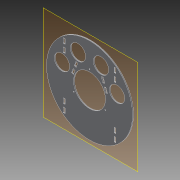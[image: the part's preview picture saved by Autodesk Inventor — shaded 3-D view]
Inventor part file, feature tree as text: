
AUTODESK INVENTOR PART (.ipt)
format: ipt  version: 2022 (Build 260153000, 153)  size: 220,160 bytes
history: native  units: mm
features: other x5, sketch x3, extrude x2, hole x1, pattern_circular x1, reference x1
ambient origin geometry x8: Origin, YZ Plane, XZ Plane, XY Plane, X Axis, Y Axis, Z Axis, Center Point
bodies: Body1 (feature_tree)
feature tree (13):
  other  "Твердое тело1"
  other  "РабПлоскость1"
  extrude  "Выдавливание1"  TaperAngle=90.0deg  [1 undecoded]
  hole  "Отверстие1"  [1 undecoded]
  pattern_circular  "Круговой массив1"  [2 undecoded]
  extrude  "Выдавливание2"  Depth=4.014257mm
  sketch  "Эскиз1"
  reference  "Ссылка1"
  sketch  "Эскиз2"
  sketch  "Эскиз3"
  parser-record x1  (decoder bookkeeping rows leaked as tree rows — omitted from the tree; the rows remain in map.json)
  other  "Поворотный_модуль_В5.iam"
  other  "Диск_опорный_В5:1"
note: 4 required parameter values undecoded (feature->parameter linkage not recoverable at this tier; creation-order binding heuristic only, values carry confidence <= 0.55)
note: 1 file-system path scrubbed to <path> (originals preserved in map.json)
